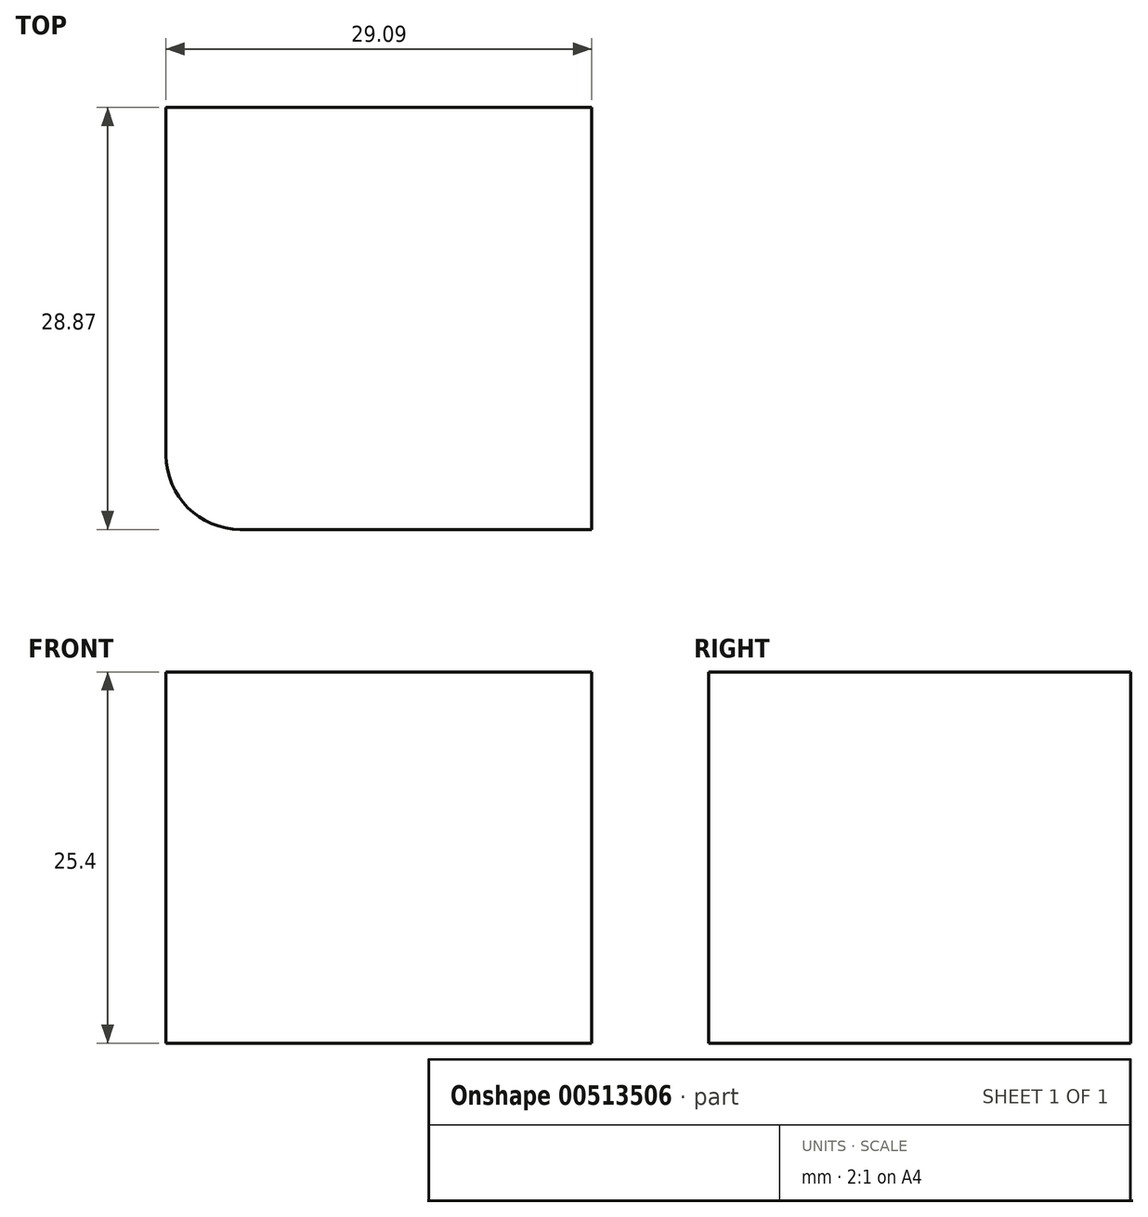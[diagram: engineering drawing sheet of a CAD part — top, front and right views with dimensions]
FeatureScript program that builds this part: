
annotation { "Feature Type Name" : "Feature", "Feature Type Description" : "" }
export const myFeature = defineFeature(function(context is Context, id is Id, definition is map)
    precondition{}
    {
        {
            var Q0;
            Q0=qCreatedBy(makeId("Top.planeOp"),FACE);
            var sketch = newSketch(context, id + "F0", { "sketchPlane" : qUnion([Q0])});
            skLineSegment(sketch, "E0.bottom", {"start": v(0, 0) * mm, "end": v(29.1, 0) * mm});
            skLineSegment(sketch, "E0.top", {"start": v(0, 28.87) * mm, "end": v(29.1, 28.87) * mm});
            skLineSegment(sketch, "E0.left", {"start": v(0, 0) * mm, "end": v(0, 28.87) * mm});
            skLineSegment(sketch, "E0.right", {"start": v(29.1, 0) * mm, "end": v(29.1, 28.87) * mm});
            skSolve(sketch);
        }
        {
            var Q0;
            Q0=makeQuery(id+"F0.imprint","IMPRINT",FACE,{"disambiguationData":[TD([[makeQuery(id+"F0.imprint","IMPRINT",EDGE,{"derivedFrom":sQuery(id+"F0.wireOp",EDGE,"E0.bottom")}),1.0]])]});
            extrude(context, id + "F1", {"entities" : qUnion([Q0]), "depth" : 25.4 * mm});
        }
        {
            var Q0;
            Q0=makeQuery(id+"F1.opExtrude","SWEPT_EDGE",EDGE,{"disambiguationData":[OSD([sQuery(id+"F0.wireOp",EDGE,"E0.bottom"),sQuery(id+"F0.wireOp",EDGE,"E0.left")])]});
            fillet(context, id + "F2", {"entities" : qUnion([Q0]), "radius" : 5.08 * mm, "tangentPropagation" : true, "allowEdgeOverflow" : false});
        }
    });
